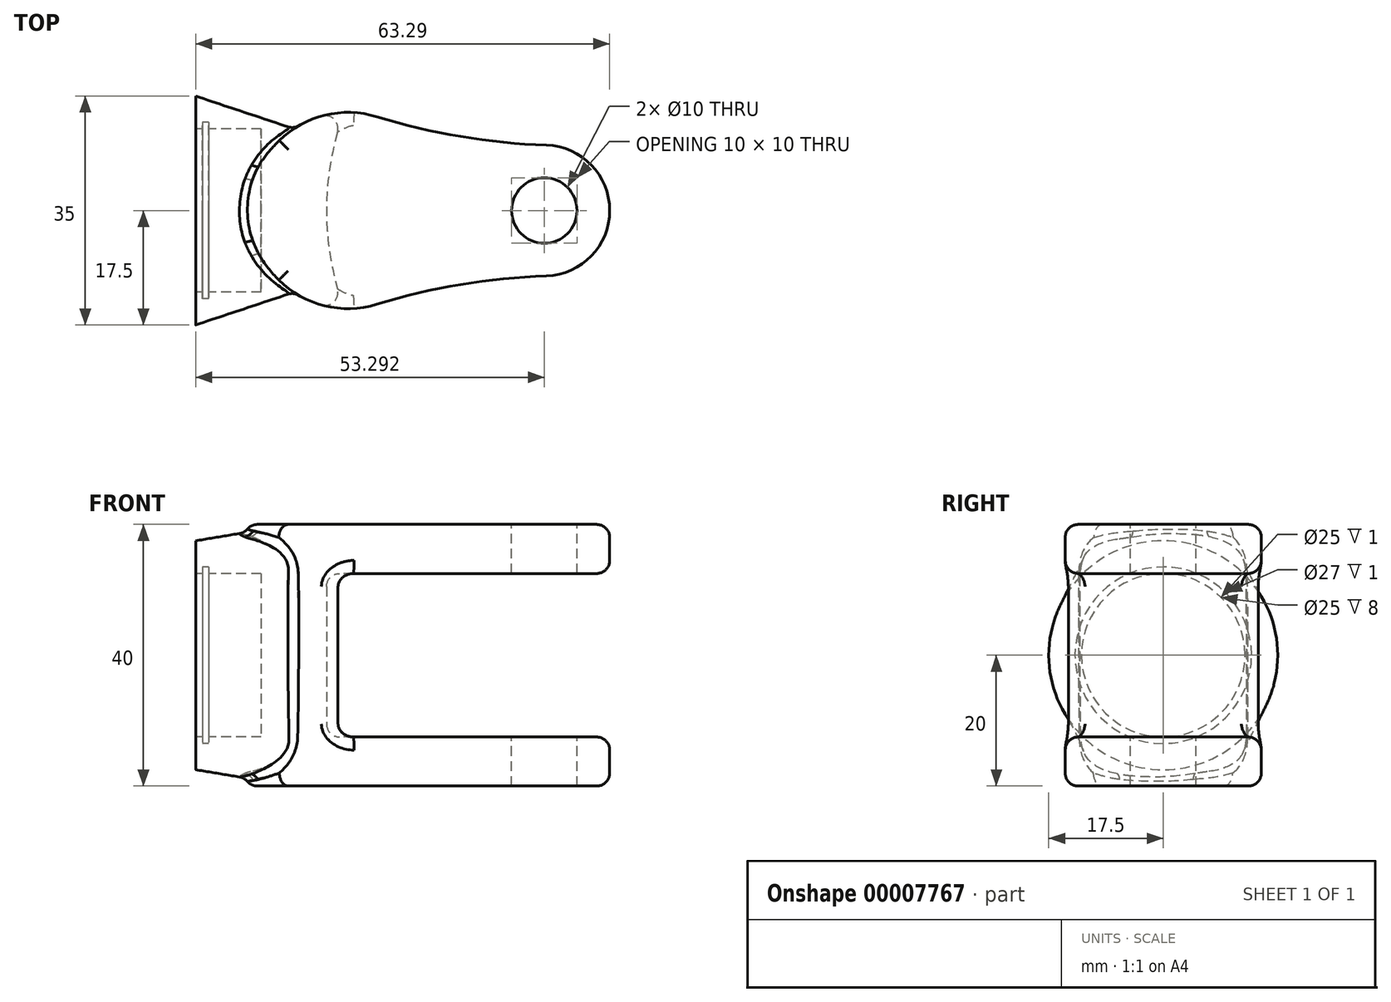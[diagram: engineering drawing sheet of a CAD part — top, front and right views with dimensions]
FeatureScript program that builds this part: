
annotation { "Feature Type Name" : "Feature", "Feature Type Description" : "" }
export const myFeature = defineFeature(function(context is Context, id is Id, definition is map)
    precondition{}
    {
        {
            var Q0;
            Q0=qCreatedBy(makeId("Right.planeOp"),FACE);
            var sketch = newSketch(context, id + "F0", { "sketchPlane" : qUnion([Q0])});
            skCircle(sketch, "E0", {"center": v(0, 0) * mm, "radius": 17.5 * mm});
            skSolve(sketch);
        }
        {
            var Q0;
            Q0=qCreatedBy(makeId("Right.planeOp"),FACE);
            cPlane(context, id + "F1", {"entities" : qUnion([Q0]), "cplaneType" : CPlaneType.OFFSET, "offset" : 15 * mm, "width" : 150 * mm, "height" : 150 * mm});
        }
        {
            var Q0;
            Q0=qCreatedBy(id+"F1.planeOp",FACE);
            var sketch = newSketch(context, id + "F2", { "sketchPlane" : qUnion([Q0])});
            skLineSegment(sketch, "E1.rect.bottom", {"start": v(-5, -20) * mm, "end": v(5, -20) * mm});
            skLineSegment(sketch, "E1.rect.top", {"start": v(-5, 20) * mm, "end": v(5, 20) * mm});
            skLineSegment(sketch, "E1.rect.left", {"start": v(-12.5, -12.5) * mm, "end": v(-12.5, 12.5) * mm});
            skLineSegment(sketch, "E1.rect.right", {"start": v(12.5, -12.5) * mm, "end": v(12.5, 12.5) * mm});
            skPoint(sketch, "E1.rect.middle", {"position": v(0, 0) * mm});
            skPoint(sketch, "E2.visualSharp", {"position": v(-12.5, 20) * mm});
            skArc(sketch, "E2.filletArc", {"start": v(-5, 20) * mm, "mid": v(-10.3, 17.8) * mm, "end": v(-12.5, 12.5) * mm});
            skPoint(sketch, "E3.visualSharp", {"position": v(12.5, 20) * mm});
            skArc(sketch, "E3.filletArc", {"start": v(12.5, 12.5) * mm, "mid": v(10.3, 17.8) * mm, "end": v(5, 20) * mm});
            skPoint(sketch, "E4.visualSharp", {"position": v(12.5, -20) * mm});
            skArc(sketch, "E4.filletArc", {"start": v(5, -20) * mm, "mid": v(10.3, -17.8) * mm, "end": v(12.5, -12.5) * mm});
            skPoint(sketch, "E5.visualSharp", {"position": v(-12.5, -20) * mm});
            skArc(sketch, "E5.filletArc", {"start": v(-12.5, -12.5) * mm, "mid": v(-10.3, -17.8) * mm, "end": v(-5, -20) * mm});
            skSolve(sketch);
        }
        {
            var Q0;
            Q0=makeQuery(id+"F0.imprint","IMPRINT",FACE,{"disambiguationData":[TD([[makeQuery(id+"F0.imprint","IMPRINT",EDGE,{"derivedFrom":sQuery(id+"F0.wireOp",EDGE,"E0")}),1.0]])]});
            var Q1;
            Q1=makeQuery(id+"F2.imprint","IMPRINT",FACE,{"disambiguationData":[TD([[makeQuery(id+"F2.imprint","IMPRINT",EDGE,{"derivedFrom":sQuery(id+"F2.wireOp",EDGE,"E1.rect.bottom")}),1.0]])]});
            loft(context, id + "F3", {"sheetProfilesArray" : [{ "sheetProfileEntities" : qUnion([Q0]) }, { "sheetProfileEntities" : qUnion([Q1]) }]});
        }
        {
            var Q0;
            Q0=qCreatedBy(makeId("Top.planeOp"),FACE);
            var sketch = newSketch(context, id + "F4", { "sketchPlane" : qUnion([Q0])});
            skArc(sketch, "E6", {"start": v(27.7, 14.34) * mm, "mid": v(8.3, 0) * mm, "end": v(27.7, -14.34) * mm});
            skArc(sketch, "E7", {"start": v(53.63, -10) * mm, "mid": v(63.3, 0) * mm, "end": v(53.63, 10) * mm});
            skArc(sketch, "E8", {"start": v(53.63, -10) * mm, "mid": v(40.52, -11.31) * mm, "end": v(27.7, -14.34) * mm});
            skLineSegment(sketch, "E9", {"start": v(53.3, 0) * mm, "end": v(23.3, 0) * mm, "construction": true});
            skArc(sketch, "E10.0.MirrorCS", {"start": v(53.63, 10) * mm, "mid": v(40.52, 11.31) * mm, "end": v(27.7, 14.34) * mm});
            skSolve(sketch);
        }
        {
            var Q0;
            Q0 = qSketchRegion(id + "F4", true);
            extrude(context, id + "F5", {"entities" : qUnion([Q0]), "operationType" : NewBodyOperationType.ADD, "endBound" : BoundingType.SYMMETRIC, "depth" : 40 * mm});
        }
        {
            var Q0;
            Q0=qCreatedBy(makeId("Front.planeOp"),FACE);
            var sketch = newSketch(context, id + "F6", { "sketchPlane" : qUnion([Q0])});
            skLineSegment(sketch, "E11.rect.bottom", {"start": v(63.3, 12.5) * mm, "end": v(20, 12.5) * mm});
            skLineSegment(sketch, "E11.rect.top", {"start": v(63.3, -12.5) * mm, "end": v(20, -12.5) * mm});
            skLineSegment(sketch, "E11.rect.right", {"start": v(20, 12.5) * mm, "end": v(20, -12.5) * mm});
            skPoint(sketch, "E11.rect.middle", {"position": v(53.63, 0) * mm});
            skLineSegment(sketch, "E12", {"start": v(63.3, 12.5) * mm, "end": v(63.3, -12.5) * mm});
            skPoint(sketch, "E11.rect.left.start.orphan", {"position": v(87.26, 12.5) * mm});
            skPoint(sketch, "E13.orphan", {"position": v(87.26, -12.5) * mm});
            skPoint(sketch, "E14.orphan", {"position": v(63.3, 20) * mm});
            skPoint(sketch, "E15.orphan", {"position": v(63.3, -20) * mm});
            skSolve(sketch);
        }
        {
            var Q0;
            Q0 = qSketchRegion(id + "F6", true);
            var Q1;
            Q1=sQuery(id+"F6.wireOp",EDGE,"E12");
            revolve(context, id + "F7", {"operationType" : NewBodyOperationType.REMOVE, "entities" : qUnion([Q0]), "axis" : qUnion([Q1]), "revolveType" : RevolveType.FULL, "oppositeDirection" : true});
        }
        {
            var Q0;
            Q0=makeQuery(id+"F3.opLoft","CAP_FACE",FACE,{"disambiguationData":[OSD([makeQuery(id+"F0.imprint","IMPRINT",FACE,{"disambiguationData":[TD([[makeQuery(id+"F0.imprint","IMPRINT",EDGE,{"derivedFrom":sQuery(id+"F0.wireOp",EDGE,"E0")}),1.0]])]})])],"isStart":true});
            var sketch = newSketch(context, id + "F8", { "sketchPlane" : qUnion([Q0])});
            skCircle(sketch, "E16", {"center": v(0, 0) * mm, "radius": 12.5 * mm});
            skSolve(sketch);
        }
        {
            var Q0;
            Q0 = qSketchRegion(id + "F8", true);
            extrude(context, id + "F9", {"entities" : qUnion([Q0]), "operationType" : NewBodyOperationType.REMOVE, "oppositeDirection" : true, "depth" : 10 * mm});
        }
        {
            var Q0;
            Q0=makeQuery(id+"F3.opLoft","CAP_FACE",FACE,{"disambiguationData":[OSD([makeQuery(id+"F0.imprint","IMPRINT",FACE,{"disambiguationData":[TD([[makeQuery(id+"F0.imprint","IMPRINT",EDGE,{"derivedFrom":sQuery(id+"F0.wireOp",EDGE,"E0")}),1.0]])]})])],"isStart":true});
            cPlane(context, id + "F10", {"entities" : qUnion([Q0]), "cplaneType" : CPlaneType.OFFSET, "offset" : 1 * mm, "oppositeDirection" : true, "width" : 150 * mm, "height" : 150 * mm});
        }
        {
            var Q0;
            Q0=qCreatedBy(id+"F10.planeOp",FACE);
            var sketch = newSketch(context, id + "F11", { "sketchPlane" : qUnion([Q0])});
            skCircle(sketch, "E17.0", {"center": v(0, 0) * mm, "radius": 12.5 * mm});
            skCircle(sketch, "E18.0", {"center": v(0, 0) * mm, "radius": 13.5 * mm});
            skSolve(sketch);
        }
        {
            var Q0;
            Q0 = qSketchRegion(id + "F11", true);
            extrude(context, id + "F12", {"entities" : qUnion([Q0]), "operationType" : NewBodyOperationType.REMOVE, "oppositeDirection" : true, "depth" : 1 * mm});
        }
        {
            var Q0;
            Q0=makeQuery(id+"F5.opExtrude","CAP_FACE",FACE,{"disambiguationData":[OSD([sQuery(id+"F4.wireOp",EDGE,"E6"),sQuery(id+"F4.wireOp",EDGE,"E7"),sQuery(id+"F4.wireOp",EDGE,"E8"),sQuery(id+"F4.wireOp",EDGE,"E10.0.MirrorCS")])],"isStart":false});
            var sketch = newSketch(context, id + "F13", { "sketchPlane" : qUnion([Q0])});
            skCircle(sketch, "E19", {"center": v(53.3, 0) * mm, "radius": 5 * mm});
            skSolve(sketch);
        }
        {
            var Q0;
            Q0 = qSketchRegion(id + "F13", true);
            extrude(context, id + "F14", {"entities" : qUnion([Q0]), "operationType" : NewBodyOperationType.REMOVE, "endBound" : BoundingType.THROUGH_ALL, "oppositeDirection" : true, "depth" : 25 * mm});
        }
        {
            var Q0;
            Q0=makeQuery(id+"F5.boolean.opBoolean","INTERSECT",EDGE,{"disambiguationData":[OD(1.0)],"derivedFrom":[makeQuery(id+"F3.opLoft","SWEPT_FACE",FACE,{"disambiguationData":[OSD([sQuery(id+"F0.wireOp",EDGE,"E0"),sQuery(id+"F2.wireOp",EDGE,"E1.rect.bottom"),sQuery(id+"F2.wireOp",EDGE,"E4.filletArc"),sQuery(id+"F2.wireOp",EDGE,"E5.filletArc")])]}),makeQuery(id+"F5.opExtrude","SWEPT_FACE",FACE,{"disambiguationData":[OSD([sQuery(id+"F4.wireOp",EDGE,"E6")])]})]});
            fillet(context, id + "F15", {"entities" : qUnion([Q0]), "radius" : 2 * mm, "tangentPropagation" : true, "allowEdgeOverflow" : false});
        }
        {
            var Q0;
            Q0=makeQuery(id+"F7.boolean.opBoolean","COPY",EDGE,{"derivedFrom":makeQuery(id+"F7.opRevolve","SWEPT_EDGE",EDGE,{"disambiguationData":[OSD([sQuery(id+"F6.wireOp",EDGE,"E11.rect.bottom"),sQuery(id+"F6.wireOp",EDGE,"E11.rect.right")])]})});
            var Q1;
            Q1=makeQuery(id+"F7.boolean.opBoolean","COPY",EDGE,{"derivedFrom":makeQuery(id+"F7.opRevolve","SWEPT_EDGE",EDGE,{"disambiguationData":[OSD([sQuery(id+"F6.wireOp",EDGE,"E11.rect.top"),sQuery(id+"F6.wireOp",EDGE,"E11.rect.right")])]})});
            fillet(context, id + "F16", {"entities" : qUnion([Q0, Q1]), "radius" : 2 * mm, "tangentPropagation" : true, "allowEdgeOverflow" : false});
        }
        {
            var Q0;
            Q0=makeQuery(id+"F7.boolean.opBoolean","INTERSECT",EDGE,{"derivedFrom":[makeQuery(id+"F5.opExtrude","SWEPT_FACE",FACE,{"disambiguationData":[OSD([sQuery(id+"F4.wireOp",EDGE,"E7")])]}),makeQuery(id+"F7.opRevolve","SWEPT_FACE",FACE,{"disambiguationData":[OSD([sQuery(id+"F6.wireOp",EDGE,"E11.rect.top")])]})]});
            var Q1;
            Q1=makeQuery(id+"F5.opExtrude","CAP_EDGE",EDGE,{"disambiguationData":[OSD([sQuery(id+"F4.wireOp",EDGE,"E7")])],"isStart":true});
            var Q2;
            Q2=makeQuery(id+"F5.opExtrude","CAP_EDGE",EDGE,{"disambiguationData":[OSD([sQuery(id+"F4.wireOp",EDGE,"E7")])],"isStart":false});
            fillet(context, id + "F17", {"entities" : qUnion([Q0, Q1, Q2]), "radius" : 2 * mm, "tangentPropagation" : true, "allowEdgeOverflow" : false});
        }
    });
